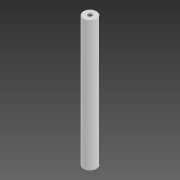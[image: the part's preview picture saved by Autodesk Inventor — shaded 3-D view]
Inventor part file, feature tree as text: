
AUTODESK INVENTOR PART (.ipt)
format: ipt  version: 2020 (Build 240168000, 168)  size: 75,264 bytes
history: native  units: in
note: dims shown in document units (in); Inventor stores cm internally (conversion verified against a paired STEP export)
features: extrude x1, sketch x1
ambient origin geometry x8: Origin, YZ Plane, XZ Plane, XY Plane, X Axis, Y Axis, Z Axis, Center Point
bodies: Solid1 (feature_tree)
feature tree (2):
  extrude  "Extrusion1"  Depth=3.937in
  sketch  "Sketch1"  dims[d0=0.3937in d1=0.1181in d2=3.937in d3=0.0in]
